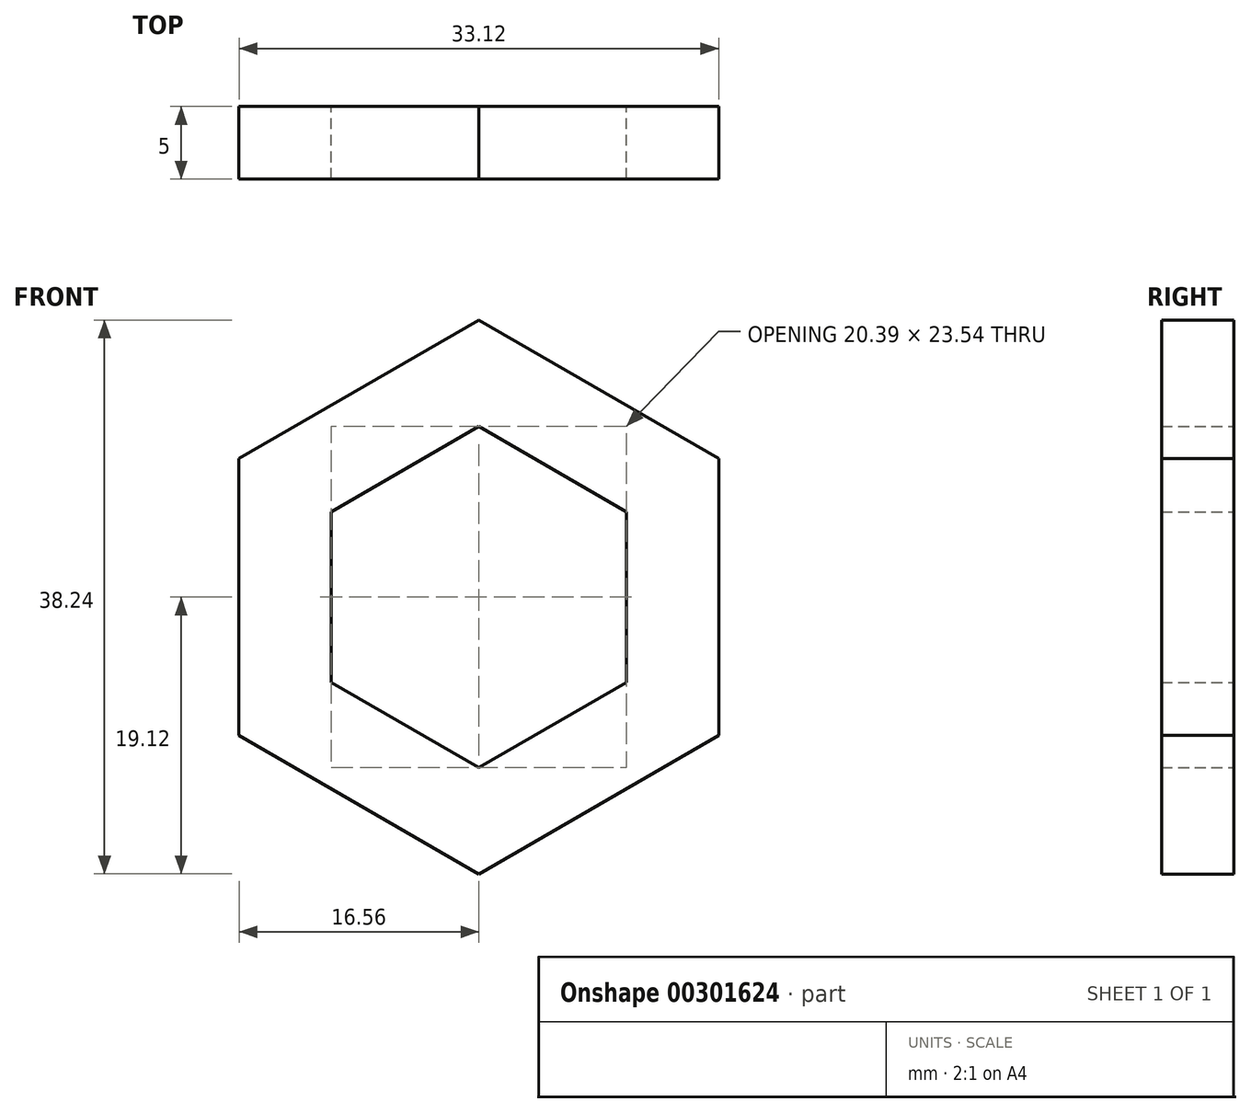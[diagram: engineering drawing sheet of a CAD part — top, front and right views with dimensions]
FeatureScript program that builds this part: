
annotation { "Feature Type Name" : "Feature", "Feature Type Description" : "" }
export const myFeature = defineFeature(function(context is Context, id is Id, definition is map)
    precondition{}
    {
        {
            var Q0;
            Q0=qCreatedBy(makeId("Front.planeOp"),FACE);
            var sketch = newSketch(context, id + "F0", { "sketchPlane" : qUnion([Q0])});
            skCircle(sketch, "E0.cCircle", {"center": v(0, 0) * mm, "radius": 16.56 * mm, "construction": true});
            skLineSegment(sketch, "E0.0", {"start": v(16.56, 9.56) * mm, "end": v(16.56, -9.56) * mm});
            skLineSegment(sketch, "E0.1", {"start": v(16.56, -9.56) * mm, "end": v(0, -19.12) * mm});
            skLineSegment(sketch, "E0.2", {"start": v(0, -19.12) * mm, "end": v(-16.56, -9.56) * mm});
            skLineSegment(sketch, "E0.3", {"start": v(-16.56, -9.56) * mm, "end": v(-16.56, 9.56) * mm});
            skLineSegment(sketch, "E0.4", {"start": v(-16.56, 9.56) * mm, "end": v(0, 19.12) * mm});
            skLineSegment(sketch, "E0.5", {"start": v(0, 19.12) * mm, "end": v(16.56, 9.56) * mm});
            skPoint(sketch, "E0.0.midPoint", {"position": v(16.56, 0) * mm});
            skCircle(sketch, "E1.cCircle", {"center": v(0, 0) * mm, "radius": 10.2 * mm, "construction": true});
            skLineSegment(sketch, "E1.0", {"start": v(10.2, -5.88) * mm, "end": v(0, -11.77) * mm});
            skLineSegment(sketch, "E1.1", {"start": v(0, -11.77) * mm, "end": v(-10.2, -5.88) * mm});
            skLineSegment(sketch, "E1.2", {"start": v(-10.2, -5.88) * mm, "end": v(-10.2, 5.88) * mm});
            skLineSegment(sketch, "E1.3", {"start": v(-10.2, 5.88) * mm, "end": v(0, 11.77) * mm});
            skLineSegment(sketch, "E1.4", {"start": v(0, 11.77) * mm, "end": v(10.2, 5.88) * mm});
            skLineSegment(sketch, "E1.5", {"start": v(10.2, 5.88) * mm, "end": v(10.2, -5.88) * mm});
            skPoint(sketch, "E1.0.midPoint", {"position": v(5.1, -8.83) * mm});
            skSolve(sketch);
        }
        {
            var Q0;
            Q0 = qSketchRegion(id + "F0", true);
            extrude(context, id + "F1", {"entities" : qUnion([Q0]), "depth" : 5 * mm});
        }
    });
